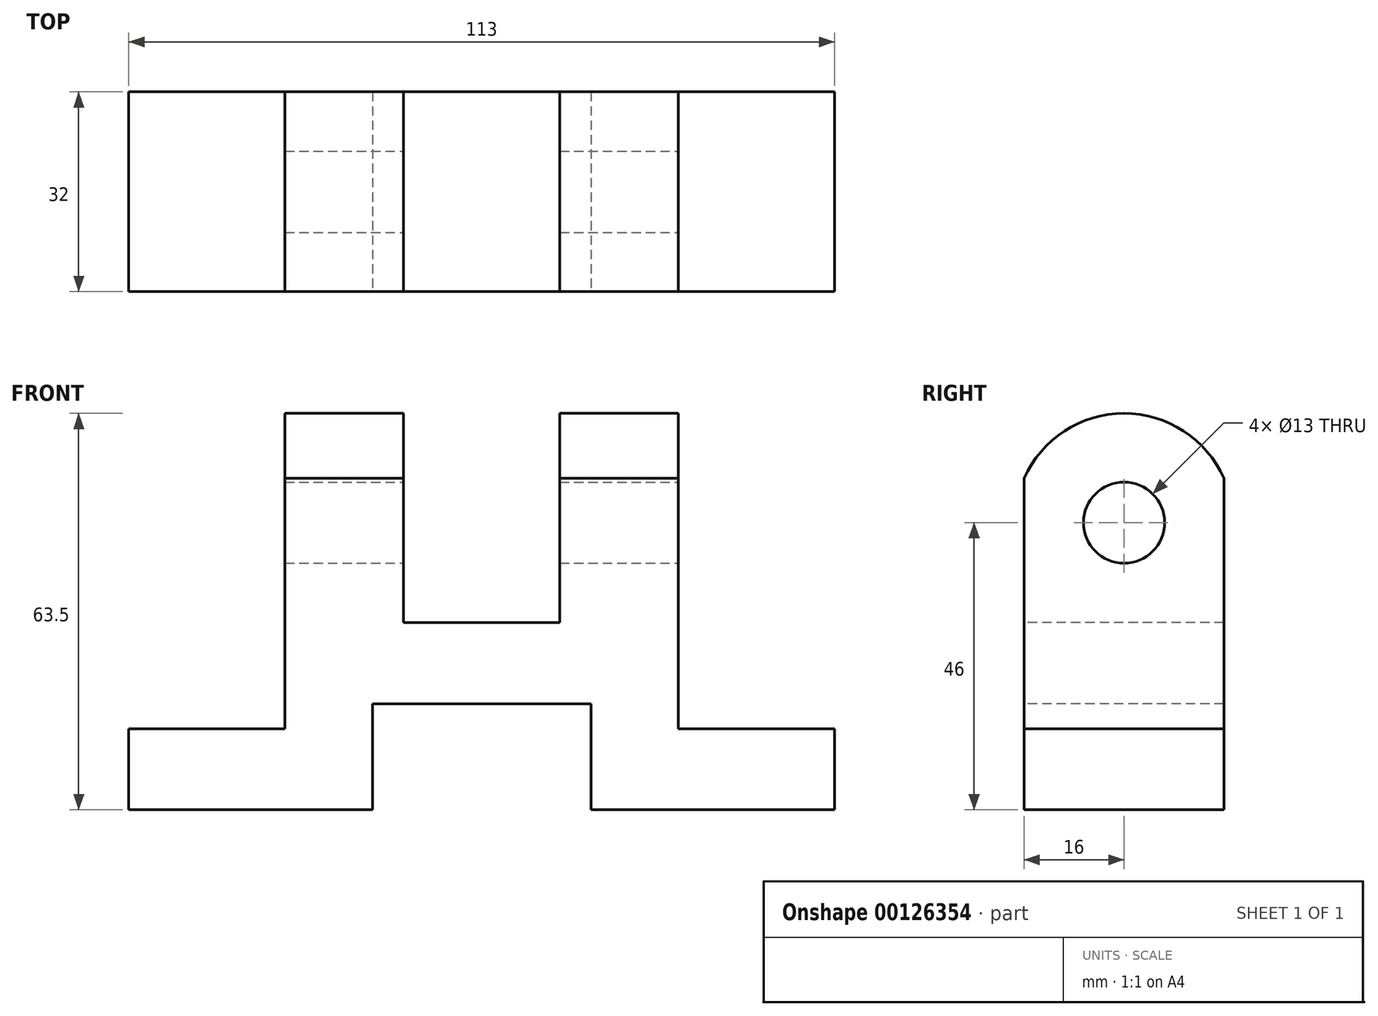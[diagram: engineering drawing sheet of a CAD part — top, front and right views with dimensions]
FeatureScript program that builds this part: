
annotation { "Feature Type Name" : "Feature", "Feature Type Description" : "" }
export const myFeature = defineFeature(function(context is Context, id is Id, definition is map)
    precondition{}
    {
        {
            var Q0;
            Q0=qCreatedBy(makeId("Front.planeOp"),FACE);
            var sketch = newSketch(context, id + "F0", { "sketchPlane" : qUnion([Q0])});
            skLineSegment(sketch, "E0.bottom", {"start": v(-56.5, 0) * mm, "end": v(56.5, 0) * mm});
            skLineSegment(sketch, "E0.top", {"start": v(-56.5, 64) * mm, "end": v(56.5, 64) * mm});
            skLineSegment(sketch, "E0.left", {"start": v(-56.5, 0) * mm, "end": v(-56.5, 64) * mm});
            skLineSegment(sketch, "E0.right", {"start": v(56.5, 0) * mm, "end": v(56.5, 64) * mm});
            skSolve(sketch);
        }
        {
            var Q0;
            Q0 = qSketchRegion(id + "F0", true);
            extrude(context, id + "F1", {"entities" : qUnion([Q0]), "oppositeDirection" : true, "depth" : 32 * mm});
        }
        {
            var Q0;
            Q0=makeQuery(id+"F1.opExtrude","SWEPT_FACE",FACE,{"disambiguationData":[OSD([sQuery(id+"F0.wireOp",EDGE,"E0.right")])]});
            var sketch = newSketch(context, id + "F2", { "sketchPlane" : qUnion([Q0])});
            skCircle(sketch, "E1", {"center": v(16, 46) * mm, "radius": 6.5 * mm});
            skArc(sketch, "E2", {"start": v(0, 53.09) * mm, "mid": v(16, 63.5) * mm, "end": v(32, 53.09) * mm});
            skLineSegment(sketch, "E3", {"start": v(32, 53.09) * mm, "end": v(32, 64) * mm});
            skLineSegment(sketch, "E4", {"start": v(32, 64) * mm, "end": v(0, 64) * mm});
            skLineSegment(sketch, "E5", {"start": v(0, 64) * mm, "end": v(0, 53.09) * mm});
            skSolve(sketch);
        }
        {
            var Q0;
            Q0 = qSketchRegion(id + "F2", true);
            extrude(context, id + "F3", {"entities" : qUnion([Q0]), "operationType" : NewBodyOperationType.REMOVE, "endBound" : BoundingType.THROUGH_ALL, "oppositeDirection" : true, "depth" : 25 * mm});
        }
        {
            var Q0;
            Q0=qCreatedBy(makeId("Front.planeOp"),FACE);
            var sketch = newSketch(context, id + "F4", { "sketchPlane" : qUnion([Q0])});
            skLineSegment(sketch, "E6.0", {"start": v(56.5, 0) * mm, "end": v(56.5, 64) * mm, "construction": true});
            skLineSegment(sketch, "E7.0", {"start": v(-56.5, 0) * mm, "end": v(56.5, 0) * mm, "construction": true});
            skPoint(sketch, "E8", {"position": v(17.5, 17) * mm});
            skPoint(sketch, "E9", {"position": v(17.5, 0) * mm});
            skLineSegment(sketch, "E10", {"start": v(17.5, 0) * mm, "end": v(17.5, 17) * mm});
            skPoint(sketch, "E11", {"position": v(-17.5, 0) * mm});
            skPoint(sketch, "E12", {"position": v(-31.5, 13) * mm});
            skPoint(sketch, "E13", {"position": v(-56.5, 13) * mm});
            skPoint(sketch, "E14", {"position": v(-56.5, 64) * mm});
            skPoint(sketch, "E15", {"position": v(31.5, 64) * mm});
            skPoint(sketch, "E16", {"position": v(56.5, 64) * mm});
            skPoint(sketch, "E17", {"position": v(56.5, 13) * mm});
            skPoint(sketch, "E18", {"position": v(31.5, 13) * mm});
            skLineSegment(sketch, "E19", {"start": v(17.5, 17) * mm, "end": v(-17.5, 17) * mm});
            skLineSegment(sketch, "E20", {"start": v(-17.5, 17) * mm, "end": v(-17.5, 0) * mm});
            skLineSegment(sketch, "E21", {"start": v(-56.5, 13) * mm, "end": v(-31.5, 13) * mm});
            skLineSegment(sketch, "E22", {"start": v(-31.5, 13) * mm, "end": v(-31.5, 64) * mm});
            skLineSegment(sketch, "E23", {"start": v(-56.5, 64) * mm, "end": v(-56.5, 13) * mm});
            skLineSegment(sketch, "E24", {"start": v(31.5, 13) * mm, "end": v(56.5, 13) * mm});
            skLineSegment(sketch, "E25", {"start": v(31.5, 64) * mm, "end": v(31.5, 13) * mm});
            skLineSegment(sketch, "E26", {"start": v(31.5, 64) * mm, "end": v(56.5, 64) * mm});
            skLineSegment(sketch, "E27", {"start": v(56.5, 13) * mm, "end": v(56.5, 64) * mm, "construction": true});
            skLineSegment(sketch, "E28", {"start": v(56.5, 13) * mm, "end": v(56.5, 64) * mm});
            skLineSegment(sketch, "E29", {"start": v(-31.5, 64) * mm, "end": v(-56.5, 64) * mm});
            skLineSegment(sketch, "E30", {"start": v(-17.5, 0) * mm, "end": v(17.5, 0) * mm});
            skPoint(sketch, "E31", {"position": v(-12.5, 64) * mm});
            skPoint(sketch, "E32", {"position": v(-12.5, 30) * mm});
            skPoint(sketch, "E33", {"position": v(12.5, 64) * mm});
            skLineSegment(sketch, "E34", {"start": v(-12.5, 30) * mm, "end": v(-12.5, 64) * mm});
            skLineSegment(sketch, "E35", {"start": v(12.5, 64) * mm, "end": v(12.5, 30) * mm});
            skLineSegment(sketch, "E36", {"start": v(12.5, 30) * mm, "end": v(-12.5, 30) * mm});
            skLineSegment(sketch, "E37", {"start": v(-12.5, 64) * mm, "end": v(12.5, 64) * mm});
            skLineSegment(sketch, "E38", {"start": v(-56.5, 64) * mm, "end": v(56.5, 64) * mm, "construction": true});
            skSolve(sketch);
        }
        {
            var Q0;
            Q0 = qSketchRegion(id + "F4", true);
            extrude(context, id + "F5", {"entities" : qUnion([Q0]), "operationType" : NewBodyOperationType.REMOVE, "endBound" : BoundingType.THROUGH_ALL, "oppositeDirection" : true, "depth" : 25 * mm});
        }
    });
